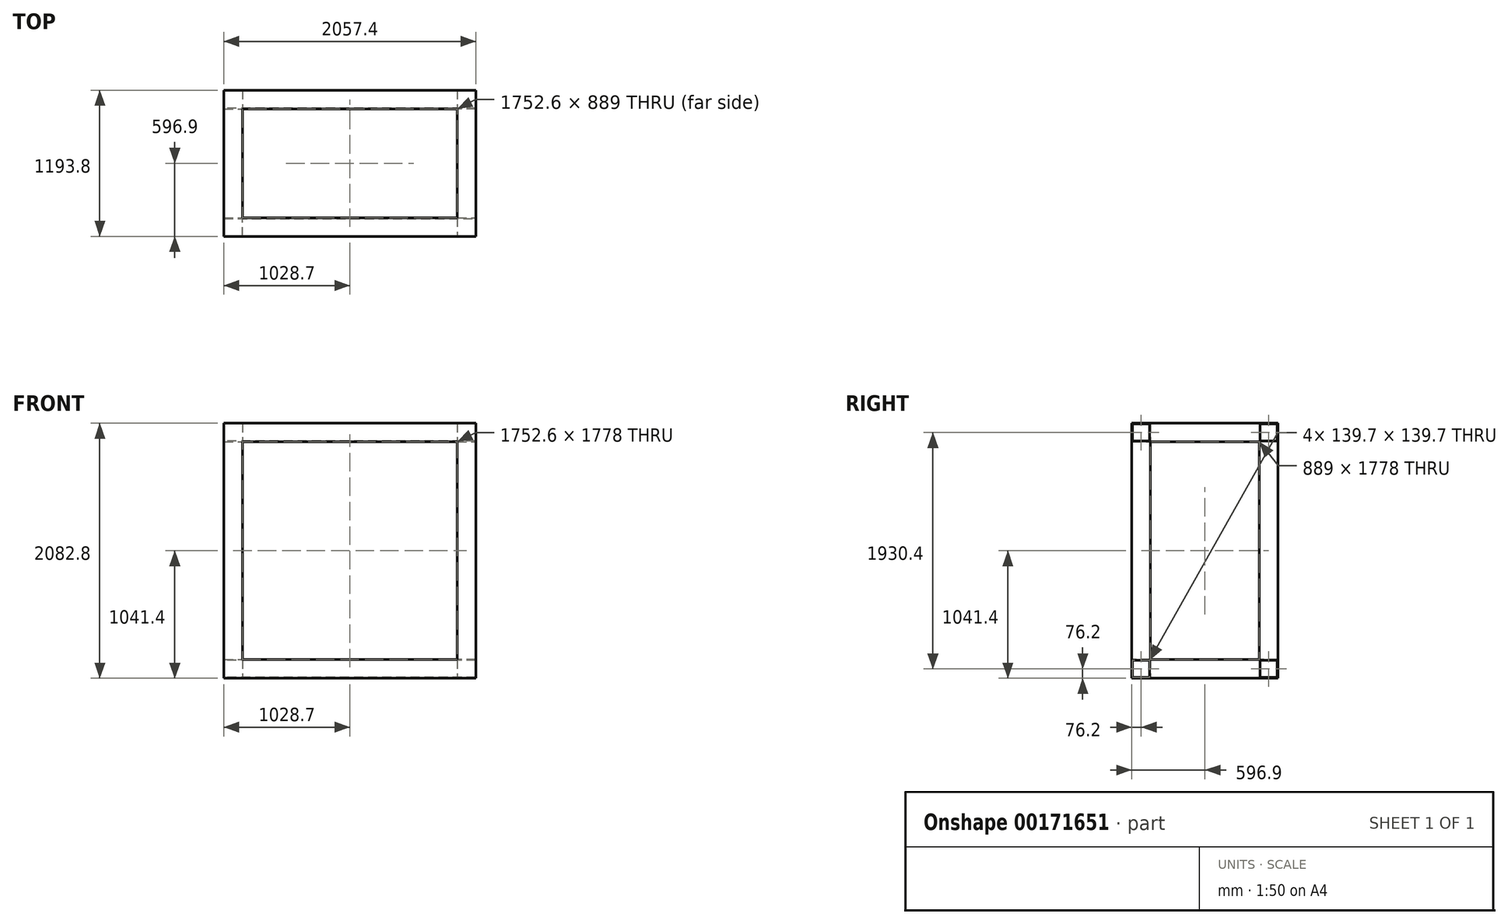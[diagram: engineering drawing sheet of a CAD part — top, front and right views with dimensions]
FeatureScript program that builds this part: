
annotation { "Feature Type Name" : "Feature", "Feature Type Description" : "" }
export const myFeature = defineFeature(function(context is Context, id is Id, definition is map)
    precondition{}
    {
        {
            var Q0;
            Q0=qCreatedBy(makeId("Right.planeOp"),FACE);
            var sketch = newSketch(context, id + "F0", { "sketchPlane" : qUnion([Q0])});
            skLineSegment(sketch, "E0.bottom", {"start": v(-76.2, 76.2) * mm, "end": v(76.2, 76.2) * mm});
            skLineSegment(sketch, "E0.top", {"start": v(-76.2, -76.2) * mm, "end": v(76.2, -76.2) * mm});
            skLineSegment(sketch, "E0.left", {"start": v(-76.2, 76.2) * mm, "end": v(-76.2, -76.2) * mm});
            skLineSegment(sketch, "E0.right", {"start": v(76.2, 76.2) * mm, "end": v(76.2, -76.2) * mm});
            skLineSegment(sketch, "E1.bottom", {"start": v(-69.85, 69.85) * mm, "end": v(69.85, 69.85) * mm});
            skLineSegment(sketch, "E1.top", {"start": v(-69.85, -69.85) * mm, "end": v(69.85, -69.85) * mm});
            skLineSegment(sketch, "E1.left", {"start": v(-69.85, 69.85) * mm, "end": v(-69.85, -69.85) * mm});
            skLineSegment(sketch, "E1.right", {"start": v(69.85, 69.85) * mm, "end": v(69.85, -69.85) * mm});
            skSolve(sketch);
        }
        {
            var Q0;
            Q0=makeQuery(id+"F0.imprint","IMPRINT",FACE,{"disambiguationData":[TD([[makeQuery(id+"F0.imprint","IMPRINT",EDGE,{"derivedFrom":sQuery(id+"F0.wireOp",EDGE,"E0.bottom")}),-1.0]])]});
            extrude(context, id + "F1", {"entities" : qUnion([Q0]), "depth" : 2057.4 * mm});
        }
        {
            var Q0;
            Q0=makeQuery(id+"F1.opExtrude","SWEPT_FACE",FACE,{"disambiguationData":[OSD([sQuery(id+"F0.wireOp",EDGE,"E0.left")])]});
            var sketch = newSketch(context, id + "F2", { "sketchPlane" : qUnion([Q0])});
            skLineSegment(sketch, "E2.bottom", {"start": v(0, 76.2) * mm, "end": v(152.4, 76.2) * mm});
            skLineSegment(sketch, "E2.top", {"start": v(0, -76.2) * mm, "end": v(152.4, -76.2) * mm});
            skLineSegment(sketch, "E2.left", {"start": v(0, 76.2) * mm, "end": v(0, -76.2) * mm});
            skLineSegment(sketch, "E2.right", {"start": v(152.4, 76.2) * mm, "end": v(152.4, -76.2) * mm});
            skLineSegment(sketch, "E3.bottom", {"start": v(2057.4, 76.2) * mm, "end": v(1905, 76.2) * mm});
            skLineSegment(sketch, "E3.top", {"start": v(2057.4, -76.2) * mm, "end": v(1905, -76.2) * mm});
            skLineSegment(sketch, "E3.left", {"start": v(2057.4, 76.2) * mm, "end": v(2057.4, -76.2) * mm});
            skLineSegment(sketch, "E3.right", {"start": v(1905, 76.2) * mm, "end": v(1905, -76.2) * mm});
            skSolve(sketch);
        }
        {
            var Q0;
            Q0=makeQuery(id+"F2.imprint","IMPRINT",FACE,{"disambiguationData":[TD([[makeQuery(id+"F2.imprint","IMPRINT",EDGE,{"derivedFrom":sQuery(id+"F2.wireOp",EDGE,"E2.bottom")}),1.0]])]});
            var Q1;
            Q1=makeQuery(id+"F2.imprint","IMPRINT",FACE,{"disambiguationData":[TD([[makeQuery(id+"F2.imprint","IMPRINT",EDGE,{"derivedFrom":sQuery(id+"F2.wireOp",EDGE,"E3.bottom")}),1.0]])]});
            extrude(context, id + "F3", {"entities" : qUnion([Q0, Q1]), "operationType" : NewBodyOperationType.ADD, "depth" : 1041.4 * mm});
        }
        {
            var Q0;
            Q0=makeQuery(id+"F3.opExtrude","SWEPT_FACE",FACE,{"disambiguationData":[OSD([sQuery(id+"F2.wireOp",EDGE,"E2.right")])]});
            var sketch = newSketch(context, id + "F4", { "sketchPlane" : qUnion([Q0])});
            skLineSegment(sketch, "E4.bottom", {"start": v(-1117.6, 76.2) * mm, "end": v(-965.2, 76.2) * mm});
            skLineSegment(sketch, "E4.top", {"start": v(-1117.6, -76.2) * mm, "end": v(-965.2, -76.2) * mm});
            skLineSegment(sketch, "E4.left", {"start": v(-1117.6, 76.2) * mm, "end": v(-1117.6, -76.2) * mm});
            skLineSegment(sketch, "E4.right", {"start": v(-965.2, 76.2) * mm, "end": v(-965.2, -76.2) * mm});
            skSolve(sketch);
        }
        {
            var Q0;
            Q0=makeQuery(id+"F4.imprint","IMPRINT",FACE,{"disambiguationData":[TD([[makeQuery(id+"F4.imprint","IMPRINT",EDGE,{"derivedFrom":sQuery(id+"F4.wireOp",EDGE,"E4.bottom")}),-1.0]])]});
            extrude(context, id + "F5", {"entities" : qUnion([Q0]), "operationType" : NewBodyOperationType.ADD, "depth" : 1752.6 * mm});
        }
        {
            var Q0;
            Q0=makeQuery(id+"F3.boolean.opBoolean","MERGE",FACE,{"derivedFrom":[makeQuery(id+"F1.opExtrude","CAP_FACE",FACE,{"disambiguationData":[OSD([sQuery(id+"F0.wireOp",EDGE,"E0.bottom"),sQuery(id+"F0.wireOp",EDGE,"E0.top"),sQuery(id+"F0.wireOp",EDGE,"E0.left"),sQuery(id+"F0.wireOp",EDGE,"E0.right"),sQuery(id+"F0.wireOp",EDGE,"E1.bottom"),sQuery(id+"F0.wireOp",EDGE,"E1.top"),sQuery(id+"F0.wireOp",EDGE,"E1.left"),sQuery(id+"F0.wireOp",EDGE,"E1.right")])],"isStart":false}),makeQuery(id+"F3.opExtrude","SWEPT_FACE",FACE,{"disambiguationData":[OSD([sQuery(id+"F2.wireOp",EDGE,"E3.left")])]})]});
            var sketch = newSketch(context, id + "F6", { "sketchPlane" : qUnion([Q0])});
            skLineSegment(sketch, "E5.bottom", {"start": v(-1111.25, 69.85) * mm, "end": v(-971.55, 69.85) * mm});
            skLineSegment(sketch, "E5.top", {"start": v(-1111.25, -69.85) * mm, "end": v(-971.55, -69.85) * mm});
            skLineSegment(sketch, "E5.left", {"start": v(-1111.25, 69.85) * mm, "end": v(-1111.25, -69.85) * mm});
            skLineSegment(sketch, "E5.right", {"start": v(-971.55, 69.85) * mm, "end": v(-971.55, -69.85) * mm});
            skSolve(sketch);
        }
        {
            var Q0;
            Q0=makeQuery(id+"F6.imprint","IMPRINT",FACE,{"disambiguationData":[TD([[makeQuery(id+"F6.imprint","IMPRINT",EDGE,{"derivedFrom":sQuery(id+"F6.wireOp",EDGE,"E5.bottom")}),-1.0]])]});
            extrude(context, id + "F7", {"entities" : qUnion([Q0]), "operationType" : NewBodyOperationType.REMOVE, "oppositeDirection" : true, "depth" : 2286 * mm});
        }
        {
            var Q0;
            Q0=makeQuery(id+"F5.boolean.opBoolean","MERGE",FACE,{"derivedFrom":[makeQuery(id+"F3.boolean.opBoolean","MERGE",FACE,{"derivedFrom":[makeQuery(id+"F1.opExtrude","SWEPT_FACE",FACE,{"disambiguationData":[OSD([sQuery(id+"F0.wireOp",EDGE,"E0.bottom")])]}),makeQuery(id+"F3.opExtrude","SWEPT_FACE",FACE,{"disambiguationData":[OSD([sQuery(id+"F2.wireOp",EDGE,"E2.bottom")])]}),makeQuery(id+"F3.opExtrude","SWEPT_FACE",FACE,{"disambiguationData":[OSD([sQuery(id+"F2.wireOp",EDGE,"E3.bottom")])]})]}),makeQuery(id+"F5.opExtrude","SWEPT_FACE",FACE,{"disambiguationData":[OSD([sQuery(id+"F4.wireOp",EDGE,"E4.bottom")])]})]});
            var sketch = newSketch(context, id + "F8", { "sketchPlane" : qUnion([Q0])});
            skLineSegment(sketch, "E6.bottom", {"start": v(0, 76.2) * mm, "end": v(152.4, 76.2) * mm});
            skLineSegment(sketch, "E6.top", {"start": v(0, -76.2) * mm, "end": v(152.4, -76.2) * mm});
            skLineSegment(sketch, "E6.left", {"start": v(0, 76.2) * mm, "end": v(0, -76.2) * mm});
            skLineSegment(sketch, "E6.right", {"start": v(152.4, 76.2) * mm, "end": v(152.4, -76.2) * mm});
            skLineSegment(sketch, "E7.bottom", {"start": v(0, -1117.6) * mm, "end": v(152.4, -1117.6) * mm});
            skLineSegment(sketch, "E7.top", {"start": v(0, -965.2) * mm, "end": v(152.4, -965.2) * mm});
            skLineSegment(sketch, "E7.left", {"start": v(0, -1117.6) * mm, "end": v(0, -965.2) * mm});
            skLineSegment(sketch, "E7.right", {"start": v(152.4, -1117.6) * mm, "end": v(152.4, -965.2) * mm});
            skLineSegment(sketch, "E8.bottom", {"start": v(1905, -965.2) * mm, "end": v(2057.4, -965.2) * mm});
            skLineSegment(sketch, "E8.top", {"start": v(1905, -1117.6) * mm, "end": v(2057.4, -1117.6) * mm});
            skLineSegment(sketch, "E8.left", {"start": v(1905, -965.2) * mm, "end": v(1905, -1117.6) * mm});
            skLineSegment(sketch, "E8.right", {"start": v(2057.4, -965.2) * mm, "end": v(2057.4, -1117.6) * mm});
            skLineSegment(sketch, "E9.bottom", {"start": v(2057.4, 76.2) * mm, "end": v(1905, 76.2) * mm});
            skLineSegment(sketch, "E9.top", {"start": v(2057.4, -76.2) * mm, "end": v(1905, -76.2) * mm});
            skLineSegment(sketch, "E9.left", {"start": v(2057.4, 76.2) * mm, "end": v(2057.4, -76.2) * mm});
            skLineSegment(sketch, "E9.right", {"start": v(1905, 76.2) * mm, "end": v(1905, -76.2) * mm});
            skSolve(sketch);
        }
        {
            var Q0;
            Q0=makeQuery(id+"F8.imprint","IMPRINT",FACE,{"disambiguationData":[TD([[makeQuery(id+"F8.imprint","IMPRINT",EDGE,{"derivedFrom":sQuery(id+"F8.wireOp",EDGE,"E6.bottom")}),1.0]])]});
            var Q1;
            Q1=makeQuery(id+"F8.imprint","IMPRINT",FACE,{"disambiguationData":[TD([[makeQuery(id+"F8.imprint","IMPRINT",EDGE,{"derivedFrom":sQuery(id+"F8.wireOp",EDGE,"E7.bottom")}),-1.0]])]});
            var Q2;
            Q2=makeQuery(id+"F8.imprint","IMPRINT",FACE,{"disambiguationData":[TD([[makeQuery(id+"F8.imprint","IMPRINT",EDGE,{"derivedFrom":sQuery(id+"F8.wireOp",EDGE,"E8.bottom")}),-1.0]])]});
            var Q3;
            Q3=makeQuery(id+"F8.imprint","IMPRINT",FACE,{"disambiguationData":[TD([[makeQuery(id+"F8.imprint","IMPRINT",EDGE,{"derivedFrom":sQuery(id+"F8.wireOp",EDGE,"E9.bottom")}),1.0]])]});
            extrude(context, id + "F9", {"entities" : qUnion([Q0, Q1, Q2, Q3]), "operationType" : NewBodyOperationType.ADD, "depth" : 1778 * mm});
        }
        {
            var Q0;
            Q0=makeQuery(id+"F9.boolean.opBoolean","MERGE",FACE,{"derivedFrom":[makeQuery(id+"F5.boolean.opBoolean","MERGE",FACE,{"derivedFrom":[makeQuery(id+"F3.opExtrude","CAP_FACE",FACE,{"disambiguationData":[OSD([sQuery(id+"F2.wireOp",EDGE,"E2.bottom"),sQuery(id+"F2.wireOp",EDGE,"E2.top"),sQuery(id+"F2.wireOp",EDGE,"E2.left"),sQuery(id+"F2.wireOp",EDGE,"E2.right")])],"isStart":false}),makeQuery(id+"F3.opExtrude","CAP_FACE",FACE,{"disambiguationData":[OSD([sQuery(id+"F2.wireOp",EDGE,"E3.bottom"),sQuery(id+"F2.wireOp",EDGE,"E3.top"),sQuery(id+"F2.wireOp",EDGE,"E3.left"),sQuery(id+"F2.wireOp",EDGE,"E3.right")])],"isStart":false}),makeQuery(id+"F5.opExtrude","SWEPT_FACE",FACE,{"disambiguationData":[OSD([sQuery(id+"F4.wireOp",EDGE,"E4.left")])]})]}),makeQuery(id+"F9.opExtrude","SWEPT_FACE",FACE,{"disambiguationData":[OSD([sQuery(id+"F8.wireOp",EDGE,"E7.bottom")])]}),makeQuery(id+"F9.opExtrude","SWEPT_FACE",FACE,{"disambiguationData":[OSD([sQuery(id+"F8.wireOp",EDGE,"E8.top")])]})]});
            var sketch = newSketch(context, id + "F10", { "sketchPlane" : qUnion([Q0])});
            skLineSegment(sketch, "E10.bottom", {"start": v(0, 2006.6) * mm, "end": v(152.4, 2006.6) * mm});
            skLineSegment(sketch, "E10.top", {"start": v(0, 1854.2) * mm, "end": v(152.4, 1854.2) * mm});
            skLineSegment(sketch, "E10.left", {"start": v(0, 2006.6) * mm, "end": v(0, 1854.2) * mm});
            skLineSegment(sketch, "E10.right", {"start": v(152.4, 2006.6) * mm, "end": v(152.4, 1854.2) * mm});
            skLineSegment(sketch, "E11.bottom", {"start": v(1905, 1854.2) * mm, "end": v(2057.4, 1854.2) * mm});
            skLineSegment(sketch, "E11.top", {"start": v(1905, 2006.6) * mm, "end": v(2057.4, 2006.6) * mm});
            skLineSegment(sketch, "E11.left", {"start": v(1905, 1854.2) * mm, "end": v(1905, 2006.6) * mm});
            skLineSegment(sketch, "E11.right", {"start": v(2057.4, 1854.2) * mm, "end": v(2057.4, 2006.6) * mm});
            skSolve(sketch);
        }
        {
            var Q0;
            Q0=makeQuery(id+"F10.imprint","IMPRINT",FACE,{"disambiguationData":[TD([[makeQuery(id+"F10.imprint","IMPRINT",EDGE,{"derivedFrom":sQuery(id+"F10.wireOp",EDGE,"E10.bottom")}),-1.0]])]});
            var Q1;
            Q1=makeQuery(id+"F10.imprint","IMPRINT",FACE,{"disambiguationData":[TD([[makeQuery(id+"F10.imprint","IMPRINT",EDGE,{"derivedFrom":sQuery(id+"F10.wireOp",EDGE,"E11.bottom")}),-1.0]])]});
            extrude(context, id + "F11", {"entities" : qUnion([Q0, Q1]), "operationType" : NewBodyOperationType.ADD, "oppositeDirection" : true, "depth" : 1193.8 * mm});
        }
        {
            var Q0;
            Q0=makeQuery(id+"F11.boolean.opBoolean","MERGE",FACE,{"derivedFrom":[makeQuery(id+"F9.opExtrude","SWEPT_FACE",FACE,{"disambiguationData":[OSD([sQuery(id+"F8.wireOp",EDGE,"E8.left")])]}),makeQuery(id+"F9.opExtrude","SWEPT_FACE",FACE,{"disambiguationData":[OSD([sQuery(id+"F8.wireOp",EDGE,"E9.right")])]}),makeQuery(id+"F11.opExtrude","SWEPT_FACE",FACE,{"disambiguationData":[OSD([sQuery(id+"F10.wireOp",EDGE,"E11.left")])]})]});
            var sketch = newSketch(context, id + "F12", { "sketchPlane" : qUnion([Q0])});
            skLineSegment(sketch, "E12.bottom", {"start": v(-76.2, 2006.6) * mm, "end": v(76.2, 2006.6) * mm});
            skLineSegment(sketch, "E12.top", {"start": v(-76.2, 1854.2) * mm, "end": v(76.2, 1854.2) * mm});
            skLineSegment(sketch, "E12.left", {"start": v(-76.2, 2006.6) * mm, "end": v(-76.2, 1854.2) * mm});
            skLineSegment(sketch, "E12.right", {"start": v(76.2, 2006.6) * mm, "end": v(76.2, 1854.2) * mm});
            skLineSegment(sketch, "E13.bottom", {"start": v(1117.6, 2006.6) * mm, "end": v(965.2, 2006.6) * mm});
            skLineSegment(sketch, "E13.top", {"start": v(1117.6, 1854.2) * mm, "end": v(965.2, 1854.2) * mm});
            skLineSegment(sketch, "E13.left", {"start": v(1117.6, 2006.6) * mm, "end": v(1117.6, 1854.2) * mm});
            skLineSegment(sketch, "E13.right", {"start": v(965.2, 2006.6) * mm, "end": v(965.2, 1854.2) * mm});
            skSolve(sketch);
        }
        {
            var Q0;
            Q0=makeQuery(id+"F12.imprint","IMPRINT",FACE,{"disambiguationData":[TD([[makeQuery(id+"F12.imprint","IMPRINT",EDGE,{"derivedFrom":sQuery(id+"F12.wireOp",EDGE,"E12.bottom")}),-1.0]])]});
            var Q1;
            Q1=makeQuery(id+"F12.imprint","IMPRINT",FACE,{"disambiguationData":[TD([[makeQuery(id+"F12.imprint","IMPRINT",EDGE,{"derivedFrom":sQuery(id+"F12.wireOp",EDGE,"E13.bottom")}),-1.0]])]});
            extrude(context, id + "F13", {"entities" : qUnion([Q0, Q1]), "operationType" : NewBodyOperationType.ADD, "depth" : 1752.6 * mm});
        }
        {
            var Q0;
            Q0=makeQuery(id+"F11.boolean.opBoolean","MERGE",FACE,{"derivedFrom":[makeQuery(id+"F9.boolean.opBoolean","MERGE",FACE,{"derivedFrom":[makeQuery(id+"F3.boolean.opBoolean","MERGE",FACE,{"derivedFrom":[makeQuery(id+"F1.opExtrude","CAP_FACE",FACE,{"disambiguationData":[OSD([sQuery(id+"F0.wireOp",EDGE,"E0.bottom"),sQuery(id+"F0.wireOp",EDGE,"E0.top"),sQuery(id+"F0.wireOp",EDGE,"E0.left"),sQuery(id+"F0.wireOp",EDGE,"E0.right"),sQuery(id+"F0.wireOp",EDGE,"E1.bottom"),sQuery(id+"F0.wireOp",EDGE,"E1.top"),sQuery(id+"F0.wireOp",EDGE,"E1.left"),sQuery(id+"F0.wireOp",EDGE,"E1.right")])],"isStart":true}),makeQuery(id+"F3.opExtrude","SWEPT_FACE",FACE,{"disambiguationData":[OSD([sQuery(id+"F2.wireOp",EDGE,"E2.left")])]})]}),makeQuery(id+"F9.opExtrude","SWEPT_FACE",FACE,{"disambiguationData":[OSD([sQuery(id+"F8.wireOp",EDGE,"E6.left")])]}),makeQuery(id+"F9.opExtrude","SWEPT_FACE",FACE,{"disambiguationData":[OSD([sQuery(id+"F8.wireOp",EDGE,"E7.left")])]})]}),makeQuery(id+"F11.opExtrude","SWEPT_FACE",FACE,{"disambiguationData":[OSD([sQuery(id+"F10.wireOp",EDGE,"E10.left")])]})]});
            var sketch = newSketch(context, id + "F14", { "sketchPlane" : qUnion([Q0])});
            skLineSegment(sketch, "E14.bottom", {"start": v(-69.85, 2000.25) * mm, "end": v(69.85, 2000.25) * mm});
            skLineSegment(sketch, "E14.top", {"start": v(-69.85, 1860.55) * mm, "end": v(69.85, 1860.55) * mm});
            skLineSegment(sketch, "E14.left", {"start": v(-69.85, 2000.25) * mm, "end": v(-69.85, 1860.55) * mm});
            skLineSegment(sketch, "E14.right", {"start": v(69.85, 2000.25) * mm, "end": v(69.85, 1860.55) * mm});
            skLineSegment(sketch, "E15.bottom", {"start": v(1111.25, 2000.25) * mm, "end": v(971.55, 2000.25) * mm});
            skLineSegment(sketch, "E15.top", {"start": v(1111.25, 1860.55) * mm, "end": v(971.55, 1860.55) * mm});
            skLineSegment(sketch, "E15.left", {"start": v(1111.25, 2000.25) * mm, "end": v(1111.25, 1860.55) * mm});
            skLineSegment(sketch, "E15.right", {"start": v(971.55, 2000.25) * mm, "end": v(971.55, 1860.55) * mm});
            skSolve(sketch);
        }
        {
            var Q0;
            Q0=makeQuery(id+"F14.imprint","IMPRINT",FACE,{"disambiguationData":[TD([[makeQuery(id+"F14.imprint","IMPRINT",EDGE,{"derivedFrom":sQuery(id+"F14.wireOp",EDGE,"E14.bottom")}),-1.0]])]});
            var Q1;
            Q1=makeQuery(id+"F14.imprint","IMPRINT",FACE,{"disambiguationData":[TD([[makeQuery(id+"F14.imprint","IMPRINT",EDGE,{"derivedFrom":sQuery(id+"F14.wireOp",EDGE,"E15.bottom")}),1.0]])]});
            extrude(context, id + "F15", {"entities" : qUnion([Q0, Q1]), "operationType" : NewBodyOperationType.REMOVE, "oppositeDirection" : true, "depth" : 2286 * mm});
        }
    });
